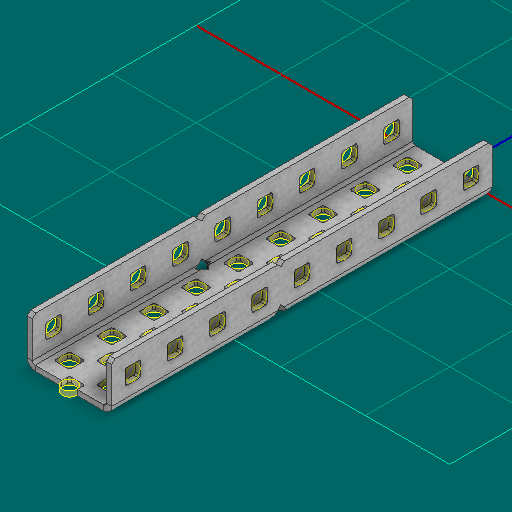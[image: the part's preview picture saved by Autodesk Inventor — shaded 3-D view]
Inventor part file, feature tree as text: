
AUTODESK INVENTOR PART (.ipt)
format: ipt  version: 2025 (Build 290162000, 162)  size: 926,208 bytes
history: native  units: in
note: dims shown in document units (in); Inventor stores cm internally (conversion verified against a paired STEP export)
features: other x96, sketch x5, sheet_metal_op x1
ambient origin geometry x8: Origin, YZ Plane, XZ Plane, XY Plane, X Axis, Y Axis, Z Axis, Center Point
bodies: Solid1 (feature_tree)
feature tree (102):
  other  "Alu C 1x2x1x9.ipt"
  other  "Solid1::Alu C 1x2x1x9.ipt"
  other  "TaggingFeature1"
  sketch  "Sketch1"  dims[d0=0.3937in]
  sketch  "Sketch2"  dims[d1=0.0625in]
  sketch  "Sketch3"
  other  "Flange Pattern Sketch"
  sketch  "Sketch9"
  sheet_metal_op  "Body Pattern Sketch"
  other  "Arc Length"
  sketch  "Sketch14"
  other  "Flange Pattern Plane"
  other  "Srf1"
  other  "Srf2"
  other  "Srf3"
  other  "Srf4"
  other  "Srf5"
  other  "Srf6"
  other  "Srf7"
  other  "Srf8"
  other  "Srf9"
  other  "Srf10"
  other  "Srf11"
  other  "Srf12"
  other  "Srf13"
  other  "Srf14"
  other  "Srf15"
  other  "Srf16"
  other  "Srf17"
  other  "Srf18"
  other  "Srf19"
  other  "Srf20"
  other  "Srf21"
  other  "Srf22"
  other  "Srf23"
  other  "Srf24"
  other  "Srf25"
  other  "Srf26"
  other  "Srf27"
  other  "Srf28"
  other  "Srf29"
  other  "Srf30"
  other  "Srf31"
  other  "Srf32"
  other  "Srf33"
  other  "Srf34"
  other  "Srf35"
  other  "Srf36"
  other  "Srf37"
  other  "Srf38"
  other  "Srf39"
  other  "Srf40"
  other  "Srf41"
  other  "Srf42"
  other  "Srf43"
  other  "Srf44"
  other  "Srf45"
  other  "Srf1::Derived"
  other  "Srf2::Derived"
  other  "Srf823::Derived"
  other  "Srf824::Derived"
  other  "Srf825::Derived"
  other  "Srf826::Derived"
  other  "Srf827::Derived"
  other  "Srf828::Derived"
  other  "Srf829::Derived"
  other  "Srf922::Derived"
  other  "Srf923::Derived"
  other  "Srf924::Derived"
  other  "Srf925::Derived"
  other  "Srf926::Derived"
  other  "Srf1143::Derived"
  other  "Srf1144::Derived"
  other  "Srf1145::Derived"
  other  "Srf1146::Derived"
  other  "Srf91::Derived"
  other  "Srf92::Derived"
  other  "Srf856::Derived"
  other  "Srf857::Derived"
  other  "Srf858::Derived"
  other  "Srf859::Derived"
  other  "Srf860::Derived"
  other  "Srf861::Derived"
  other  "Srf862::Derived"
  other  "Srf959::Derived"
  other  "Srf960::Derived"
  other  "Srf961::Derived"
  other  "Srf962::Derived"
  other  "Srf963::Derived"
  other  "Srf1199::Derived"
  other  "Srf1200::Derived"
  other  "Srf1201::Derived"
  other  "Srf1202::Derived"
  other  "Srf786::Derived"
  other  "Srf889::Derived"
  other  "Srf890::Derived"
  other  "Srf891::Derived"
  other  "Srf892::Derived"
  other  "Srf893::Derived"
  other  "Srf894::Derived"
  other  "Srf895::Derived"
  other  "Srf896::Derived"
